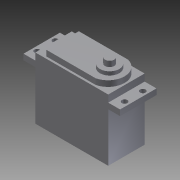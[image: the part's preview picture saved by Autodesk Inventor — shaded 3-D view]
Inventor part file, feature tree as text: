
AUTODESK INVENTOR PART (.ipt)
format: ipt  version: 2012 (Build 160160000, 160)  size: 172,032 bytes
history: native  units: mm
features: sketch x8, extrude x6, hole x2, projected_geometry x1
ambient origin geometry x8: Origin, YZ Plane, XZ Plane, XY Plane, X Axis, Y Axis, Z Axis, Center Point
bodies: Solid1 (feature_tree)
feature tree (17):
  extrude  "Extrusion1"  Depth=20.0mm
  extrude  "Extrusion2"  Depth=5.0mm
  sketch  "Sketch3"  dims[d8=27.0mm d9=27.0mm]
  extrude  "Extrusion3"  Depth=27.0mm
  extrude  "Extrusion4"  Depth=5.35mm
  sketch  "Sketch6"  dims[d15=3.15mm d16=6.5mm d17=0.0mm]
  sketch  "Sketch7"  dims[d18=7.0mm d19=3.15mm]
  sketch  "Sketch8"  dims[d20=6.5mm d21=0.0mm d22=9.25mm d25=5.0mm d26=5.0mm d35=5.0mm d36=5.0mm d37=5.0mm d38=5.0mm d42=10.636085mm d43=2.0mm d44=0.0mm d57=3.0mm d58=6.0mm d59=4.0mm d60=2.0mm d61=90.0deg d62=8.0mm d63=20.594885mm d64=3.0mm d65=6.0mm d66=4.0mm d67=2.0mm d68=90.0deg d69=8.0mm d70=20.594885mm d75=5.0mm d76=5.0mm d77=0.0mm d79=10.0mm d80=5.0mm d81=4.0mm d82=4.0mm d83=10.0mm d84=4.0mm d85=4.0mm]
  extrude  "Extrusion7"  Depth=7.0mm
  hole  "Hole1"  [1 undecoded]
  hole  "Hole2"  [1 undecoded]
  extrude  "Extrusion14"  Depth=9.25mm
  sketch  "Sketch1"  dims[d0=40.0mm d1=20.0mm]
  sketch  "Sketch2"  dims[d2=37.0mm d3=0.0mm d6=5.0mm]
  sketch  "Sketch4"  dims[d10=5.35mm d11=5.35mm]
  projected_geometry  "Projected Loop1"
  sketch  "Sketch5"  dims[d12=3.15mm d13=0.0mm d14=7.0mm]
note: 2 required parameter values undecoded (feature->parameter linkage not recoverable at this tier; creation-order binding heuristic only, values carry confidence <= 0.55)
